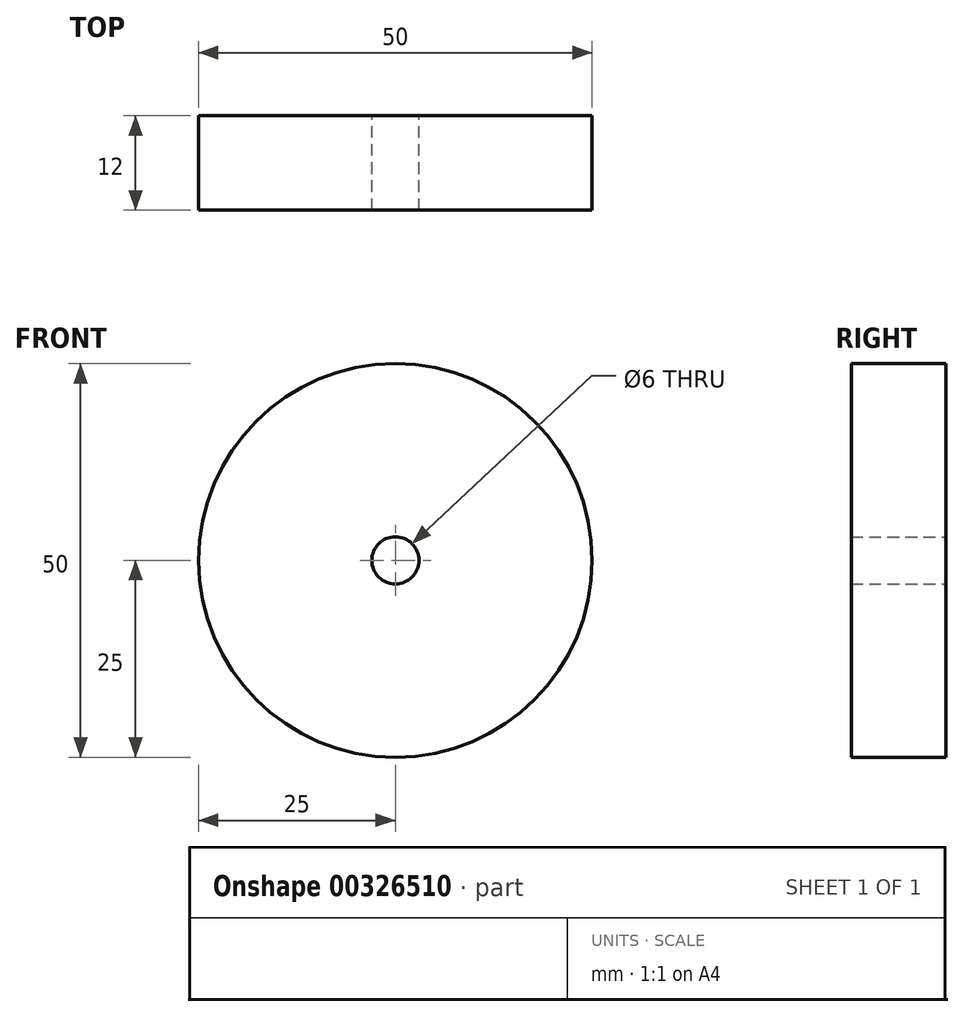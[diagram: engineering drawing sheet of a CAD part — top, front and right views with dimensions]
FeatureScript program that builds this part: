
annotation { "Feature Type Name" : "Feature", "Feature Type Description" : "" }
export const myFeature = defineFeature(function(context is Context, id is Id, definition is map)
    precondition{}
    {
        {
            var Q0;
            Q0=qCreatedBy(makeId("Front.planeOp"),FACE);
            var sketch = newSketch(context, id + "F0", { "sketchPlane" : qUnion([Q0])});
            skCircle(sketch, "E0", {"center": v(0, 0) * mm, "radius": 25 * mm});
            skCircle(sketch, "E1", {"center": v(0, 0) * mm, "radius": 3 * mm});
            skSolve(sketch);
        }
        {
            var Q0;
            Q0=makeQuery(id+"F0.imprint","IMPRINT",FACE,{"disambiguationData":[TD([[makeQuery(id+"F0.imprint","IMPRINT",EDGE,{"derivedFrom":sQuery(id+"F0.wireOp",EDGE,"E0")}),1.0]])]});
            extrude(context, id + "F1", {"entities" : qUnion([Q0]), "depth" : 12 * mm});
        }
    });
